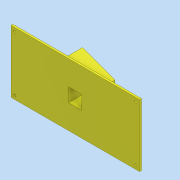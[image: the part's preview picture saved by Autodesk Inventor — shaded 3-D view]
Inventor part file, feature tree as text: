
AUTODESK INVENTOR PART (.ipt)
format: ipt  version: 2022 (Build 260153000, 153)  size: 177,152 bytes
history: native  units: mm
features: extrude x5, sketch x5
ambient origin geometry x8: Origin, YZ Plane, XZ Plane, XY Plane, X Axis, Y Axis, Z Axis, Center Point
bodies: Solid1 (feature_tree)
feature tree (10):
  extrude  "Extrusion1"  Depth=140.0mm
  extrude  "Extrusion2"  Depth=2.0mm
  extrude  "Extrusion3"  Depth=2.5mm
  extrude  "Extrusion5"  Depth=40.0mm
  extrude  "Extrusion6"  TaperAngle=15.0deg  [1 undecoded]
  sketch  "Sketch1"  dims[d0=68.0mm d1=140.0mm]
  sketch  "Sketch2"  dims[d2=2.0mm d3=0.0mm d4=4.0mm]
  sketch  "Sketch3"  dims[d5=4.0mm d6=2.5mm]
  sketch  "Sketch5"  dims[d7=48.296291mm d8=40.0mm]
  sketch  "Sketch6"  dims[d9=30.0mm d10=0.0mm d11=15.0deg d12=50.0mm d13=0.0mm d18=30.0mm d19=30.0mm d20=5.0mm d21=5.0mm d22=5.0mm d23=5.0mm d24=7.0mm d25=0.0mm d26=14.488887mm d27=15.0mm d28=7.0mm d29=0.0mm]
note: 1 required parameter value undecoded (feature->parameter linkage not recoverable at this tier; creation-order binding heuristic only, values carry confidence <= 0.55)
